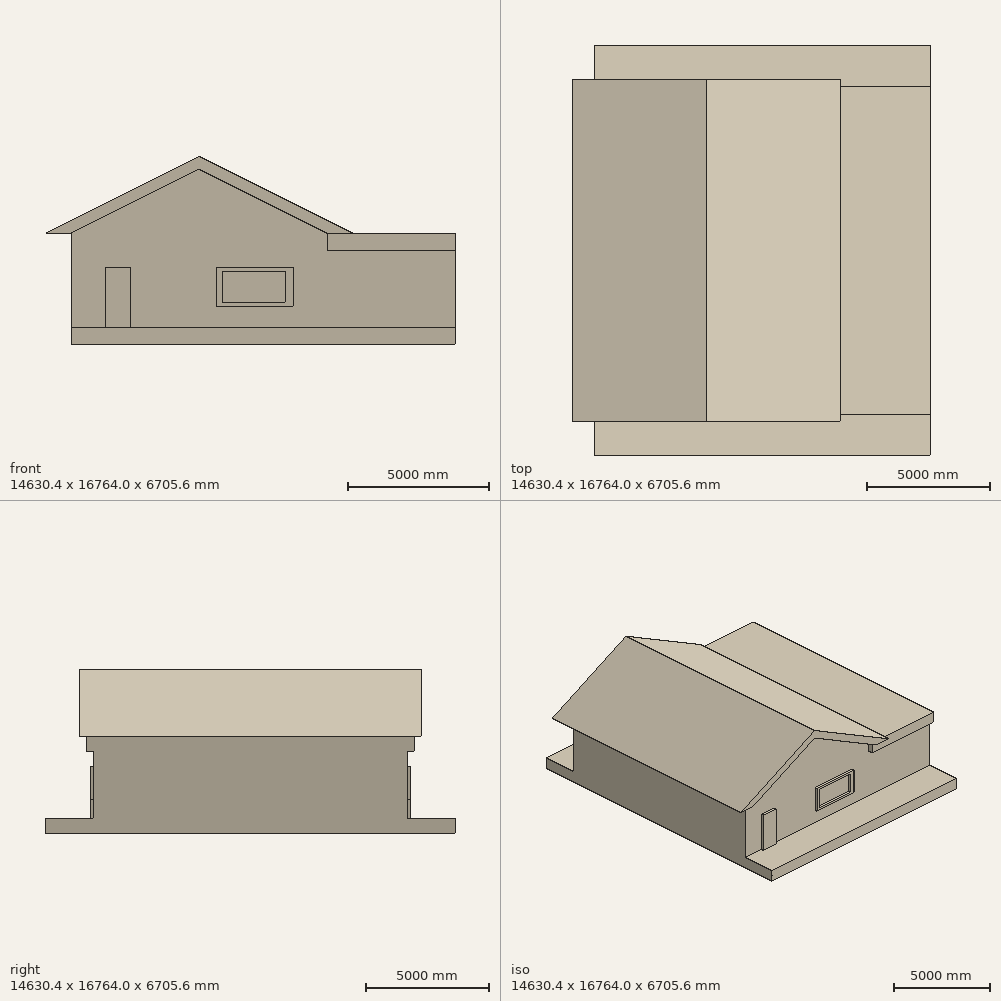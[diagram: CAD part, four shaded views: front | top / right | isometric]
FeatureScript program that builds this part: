
annotation { "Feature Type Name" : "Feature", "Feature Type Description" : "" }
export const myFeature = defineFeature(function(context is Context, id is Id, definition is map)
    precondition{}
    {
        {
            var Q0;
            Q0=qCreatedBy(makeId("Front.planeOp"),FACE);
            var sketch = newSketch(context, id + "F0", { "sketchPlane" : qUnion([Q0])});
            skLineSegment(sketch, "E0", {"start": v(0, 0) * mm, "end": v(-4572, 0) * mm});
            skLineSegment(sketch, "E1", {"start": v(0, 0) * mm, "end": v(4572, 0) * mm});
            skLineSegment(sketch, "E2", {"start": v(0, 0) * mm, "end": v(0, 2286) * mm});
            skLineSegment(sketch, "E3", {"start": v(-4572, 0) * mm, "end": v(0, 2286) * mm});
            skLineSegment(sketch, "E4", {"start": v(4572, 0) * mm, "end": v(0, 2286) * mm});
            skLineSegment(sketch, "E5", {"start": v(0, 2286) * mm, "end": v(0, 2743.2) * mm});
            skLineSegment(sketch, "E6", {"start": v(-4572, 0) * mm, "end": v(-5486.4, 0) * mm});
            skLineSegment(sketch, "E7", {"start": v(4572, 0) * mm, "end": v(5486.4, 0) * mm});
            skLineSegment(sketch, "E8", {"start": v(-5486.4, 0) * mm, "end": v(0, 2743.2) * mm});
            skLineSegment(sketch, "E9", {"start": v(5486.4, 0) * mm, "end": v(0, 2743.2) * mm});
            skLineSegment(sketch, "E10", {"start": v(-4572, 0) * mm, "end": v(-4572, -3352.8) * mm});
            skLineSegment(sketch, "E11", {"start": v(-4572, -3352.8) * mm, "end": v(-4572, -3962.4) * mm});
            skLineSegment(sketch, "E12", {"start": v(4572, 0) * mm, "end": v(4572, -3352.8) * mm});
            skLineSegment(sketch, "E13", {"start": v(4572, -3352.8) * mm, "end": v(4572, -3962.4) * mm});
            skLineSegment(sketch, "E14", {"start": v(-4572, -3352.8) * mm, "end": v(4572, -3352.8) * mm});
            skLineSegment(sketch, "E15.bottom", {"start": v(609.6, -1219.2) * mm, "end": v(3352.8, -1219.2) * mm});
            skLineSegment(sketch, "E15.top", {"start": v(609.6, -2590.8) * mm, "end": v(3352.8, -2590.8) * mm});
            skLineSegment(sketch, "E15.left", {"start": v(609.6, -1219.2) * mm, "end": v(609.6, -2590.8) * mm});
            skLineSegment(sketch, "E15.right", {"start": v(3352.8, -1219.2) * mm, "end": v(3352.8, -2590.8) * mm});
            skLineSegment(sketch, "E16", {"start": v(-4572, -3962.4) * mm, "end": v(4572, -3962.4) * mm});
            skLineSegment(sketch, "E17", {"start": v(-3352.8, -3352.8) * mm, "end": v(-3352.8, -1219.2) * mm});
            skLineSegment(sketch, "E18", {"start": v(-3352.8, -1219.2) * mm, "end": v(-2438.4, -1219.2) * mm});
            skLineSegment(sketch, "E19", {"start": v(-2438.4, -1219.2) * mm, "end": v(-2438.4, -3352.8) * mm});
            skLineSegment(sketch, "E20", {"start": v(4572, -3962.4) * mm, "end": v(9144, -3962.4) * mm});
            skLineSegment(sketch, "E21", {"start": v(9144, -3962.4) * mm, "end": v(9144, -3352.8) * mm});
            skLineSegment(sketch, "E22", {"start": v(4572, -3352.8) * mm, "end": v(9144, -3352.8) * mm});
            skLineSegment(sketch, "E23", {"start": v(4572, 0) * mm, "end": v(9144, 0) * mm});
            skPoint(sketch, "E23.endSnap0", {"position": v(5029.2, 0) * mm});
            skLineSegment(sketch, "E24", {"start": v(9144, -3352.8) * mm, "end": v(9144, 0) * mm});
            skLineSegment(sketch, "E25", {"start": v(4572, -609.6) * mm, "end": v(9144, -609.6) * mm});
            skLineSegment(sketch, "E26", {"start": v(822.96, -1341.12) * mm, "end": v(822.96, -2468.88) * mm});
            skLineSegment(sketch, "E27", {"start": v(822.96, -1341.12) * mm, "end": v(3078.48, -1341.12) * mm});
            skLineSegment(sketch, "E28", {"start": v(3078.48, -1341.12) * mm, "end": v(3078.48, -2468.88) * mm});
            skLineSegment(sketch, "E29", {"start": v(822.96, -2468.88) * mm, "end": v(3078.48, -2468.88) * mm});
            skText(sketch, "E30", { "text": "GWENDA", "fontName": "OpenSans-Regular.ttf"});
            const initialGuessF0  = {"E30": [-5.46212, 4.3843, 1, 0, 1.40102]};
            skSetInitialGuess(sketch, initialGuessF0);
            skSolve(sketch);
        }
        {
            var Q0;
            Q0=makeQuery(id+"F0.imprint","IMPRINT",FACE,{"disambiguationData":[TD([[makeQuery(id+"F0.imprint","IMPRINT",EDGE,{"derivedFrom":sQuery(id+"F0.wireOp",EDGE,"E3")}),1.0]])]});
            var Q1;
            {var subQ0=sQuery(id+"F0.wireOp",EDGE,"E4");Q1=makeQuery(id+"F0.imprint","IMPRINT",FACE,{"disambiguationData":[TD([[makeQuery(id+"F0.imprint","IMPRINT",EDGE,{"derivedFrom":subQ0}),-1.0]])]});}
            extrude(context, id + "F1", {"entities" : qUnion([Q0, Q1]), "endBound" : BoundingType.SYMMETRIC, "depth" : 863.6 * mm, "offsetDistance" : 25.4 * mm});
        }
        {
            var Q0;
            Q0=makeQuery(id+"F0.imprint","IMPRINT",FACE,{"disambiguationData":[TD([[makeQuery(id+"F0.imprint","IMPRINT",EDGE,{"derivedFrom":sQuery(id+"F0.wireOp",EDGE,"E3")}),1.0]])]});
            var Q1;
            {var subQ0=sQuery(id+"F0.wireOp",EDGE,"E4");Q1=makeQuery(id+"F0.imprint","IMPRINT",FACE,{"disambiguationData":[TD([[makeQuery(id+"F0.imprint","IMPRINT",EDGE,{"derivedFrom":subQ0}),-1.0]])]});}
            extrude(context, id + "F2", {"entities" : qUnion([Q0, Q1]), "operationType" : NewBodyOperationType.ADD, "endBound" : BoundingType.SYMMETRIC, "depth" : 14020.8 * mm, "offsetDistance" : 30.48 * mm});
        }
        {
            var Q0;
            Q0=makeQuery(id+"F0.imprint","IMPRINT",FACE,{"disambiguationData":[TD([[makeQuery(id+"F0.imprint","IMPRINT",EDGE,{"derivedFrom":sQuery(id+"F0.wireOp",EDGE,"E1")}),1.0]])]});
            var Q1;
            Q1=makeQuery(id+"F0.imprint","IMPRINT",FACE,{"disambiguationData":[TD([[makeQuery(id+"F0.imprint","IMPRINT",EDGE,{"derivedFrom":sQuery(id+"F0.wireOp",EDGE,"E0")}),-1.0]])]});
            extrude(context, id + "F3", {"entities" : qUnion([Q0, Q1]), "operationType" : NewBodyOperationType.ADD, "endBound" : BoundingType.SYMMETRIC, "depth" : 12801.6 * mm, "offsetDistance" : 30.48 * mm});
        }
        {
            var Q0;
            Q0=makeQuery(id+"F0.imprint","IMPRINT",FACE,{"disambiguationData":[TD([[makeQuery(id+"F0.imprint","IMPRINT",EDGE,{"derivedFrom":sQuery(id+"F0.wireOp",EDGE,"E0")}),1.0]])]});
            extrude(context, id + "F4", {"entities" : qUnion([Q0]), "operationType" : NewBodyOperationType.ADD, "endBound" : BoundingType.SYMMETRIC, "depth" : 12801.6 * mm, "offsetDistance" : 30.48 * mm});
        }
        {
            var Q0;
            {var subQ0=sQuery(id+"F0.wireOp",EDGE,"E17");Q0=makeQuery(id+"F0.imprint","IMPRINT",FACE,{"disambiguationData":[TD([[makeQuery(id+"F0.imprint","IMPRINT",EDGE,{"derivedFrom":subQ0}),-1.0]])]});}
            extrude(context, id + "F5", {"entities" : qUnion([Q0]), "operationType" : NewBodyOperationType.ADD, "endBound" : BoundingType.SYMMETRIC, "depth" : 13106.4 * mm, "offsetDistance" : 30.48 * mm});
        }
        {
            var Q0;
            Q0=makeQuery(id+"F0.imprint","IMPRINT",FACE,{"disambiguationData":[TD([[makeQuery(id+"F0.imprint","IMPRINT",EDGE,{"derivedFrom":sQuery(id+"F0.wireOp",EDGE,"E15.bottom")}),-1.0]])]});
            extrude(context, id + "F6", {"entities" : qUnion([Q0]), "operationType" : NewBodyOperationType.ADD, "endBound" : BoundingType.SYMMETRIC, "depth" : 13106.4 * mm, "offsetDistance" : 30.48 * mm});
        }
        {
            var Q0;
            Q0=makeQuery(id+"F0.imprint","IMPRINT",FACE,{"disambiguationData":[TD([[makeQuery(id+"F0.imprint","IMPRINT",EDGE,{"derivedFrom":sQuery(id+"F0.wireOp",EDGE,"E26")}),1.0]])]});
            extrude(context, id + "F7", {"entities" : qUnion([Q0]), "operationType" : NewBodyOperationType.ADD, "endBound" : BoundingType.SYMMETRIC, "depth" : 12801.6 * mm, "offsetDistance" : 30.48 * mm});
        }
        {
            var Q0;
            {var subQ1=sQuery(id+"F0.wireOp",EDGE,"E11");Q0=makeQuery(id+"F0.imprint","IMPRINT",FACE,{"disambiguationData":[TD([[makeQuery(id+"F0.imprint","IMPRINT",EDGE,{"derivedFrom":subQ1}),1.0]])]});}
            var Q1;
            Q1=makeQuery(id+"F0.imprint","IMPRINT",FACE,{"disambiguationData":[TD([[makeQuery(id+"F0.imprint","IMPRINT",EDGE,{"derivedFrom":sQuery(id+"F0.wireOp",EDGE,"E13")}),1.0]])]});
            extrude(context, id + "F8", {"entities" : qUnion([Q0, Q1]), "operationType" : NewBodyOperationType.ADD, "endBound" : BoundingType.SYMMETRIC, "depth" : 16764 * mm, "offsetDistance" : 30.48 * mm});
        }
        {
            var Q0;
            {var subQ0=sQuery(id+"F0.wireOp",EDGE,"E22");Q0=makeQuery(id+"F0.imprint","IMPRINT",FACE,{"disambiguationData":[TD([[makeQuery(id+"F0.imprint","IMPRINT",EDGE,{"derivedFrom":subQ0}),1.0]])]});}
            extrude(context, id + "F9", {"entities" : qUnion([Q0]), "operationType" : NewBodyOperationType.ADD, "endBound" : BoundingType.SYMMETRIC, "depth" : 12801.6 * mm, "offsetDistance" : 30.48 * mm});
        }
        {
            var Q0;
            {var subQ6=sQuery(id+"F0.wireOp",EDGE,"E25");Q0=makeQuery(id+"F0.imprint","IMPRINT",FACE,{"disambiguationData":[TD([[makeQuery(id+"F0.imprint","IMPRINT",EDGE,{"derivedFrom":subQ6}),1.0]])]});}
            extrude(context, id + "F10", {"entities" : qUnion([Q0]), "operationType" : NewBodyOperationType.ADD, "endBound" : BoundingType.SYMMETRIC, "depth" : 13411.2 * mm, "offsetDistance" : 30.48 * mm});
        }
    });
